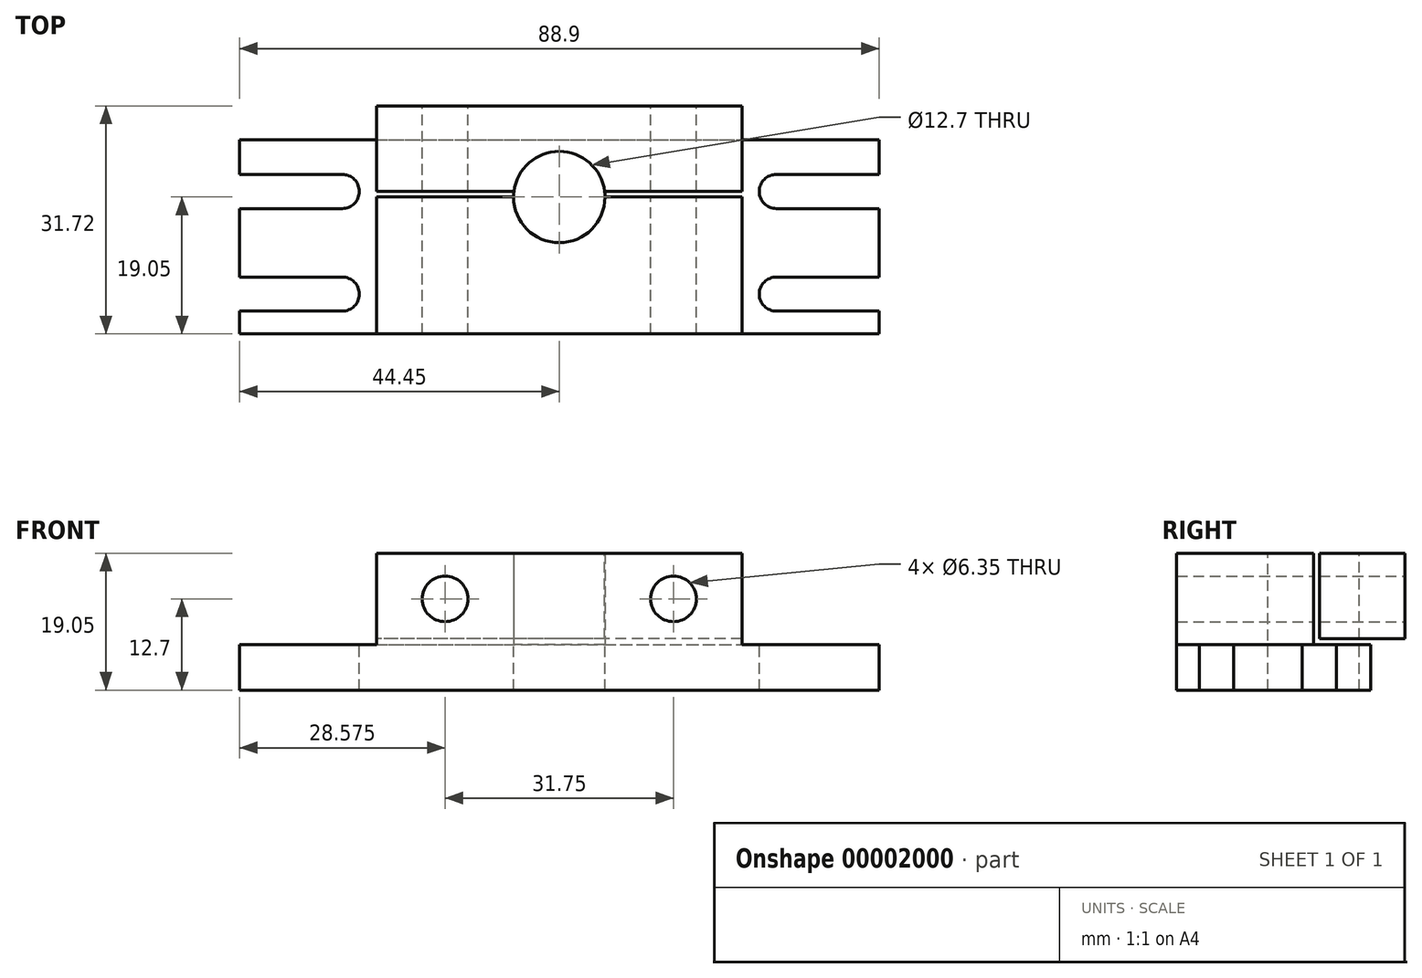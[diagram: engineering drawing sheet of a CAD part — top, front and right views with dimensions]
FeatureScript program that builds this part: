
annotation { "Feature Type Name" : "Feature", "Feature Type Description" : "" }
export const myFeature = defineFeature(function(context is Context, id is Id, definition is map)
    precondition{}
    {
        {
            var Q0;
            Q0=qCreatedBy(makeId("Top.planeOp"),FACE);
            var sketch = newSketch(context, id + "F0", { "sketchPlane" : qUnion([Q0])});
            skLineSegment(sketch, "E0.bottom", {"start": v(-44.45, 12.7) * mm, "end": v(44.45, 12.7) * mm});
            skLineSegment(sketch, "E0.top", {"start": v(-44.45, -12.7) * mm, "end": v(44.45, -12.7) * mm});
            skLineSegment(sketch, "E0.left", {"start": v(-44.45, 12.7) * mm, "end": v(-44.45, -12.7) * mm});
            skLineSegment(sketch, "E0.right", {"start": v(44.45, 12.7) * mm, "end": v(44.45, -12.7) * mm});
            skLineSegment(sketch, "E1", {"start": v(0, 12.7) * mm, "end": v(0, 0) * mm, "construction": true});
            skLineSegment(sketch, "E2", {"start": v(0, 0) * mm, "end": v(-44.45, 0) * mm, "construction": true});
            skSolve(sketch);
        }
        {
            var Q0;
            Q0=qSketchRegion(id+"F0",true);
            extrude(context, id + "F1", {"entities" : qUnion([Q0]), "depth" : 19.05 * mm});
        }
        {
            var Q0;
            Q0=makeQuery(id+"F1.opExtrude","SWEPT_FACE",FACE,{"disambiguationData":[OSD([sQuery(id+"F0.wireOp",EDGE,"E0.top")])]});
            var sketch = newSketch(context, id + "F2", { "sketchPlane" : qUnion([Q0])});
            skLineSegment(sketch, "E3.bottom", {"start": v(25.4, 19.05) * mm, "end": v(44.45, 19.05) * mm});
            skLineSegment(sketch, "E3.top", {"start": v(25.4, 6.35) * mm, "end": v(44.45, 6.35) * mm});
            skLineSegment(sketch, "E3.left", {"start": v(25.4, 19.05) * mm, "end": v(25.4, 6.35) * mm});
            skLineSegment(sketch, "E3.right", {"start": v(44.45, 19.05) * mm, "end": v(44.45, 6.35) * mm});
            skLineSegment(sketch, "E4.0.MirrorCS", {"start": v(-44.45, 19.05) * mm, "end": v(-44.45, 6.35) * mm});
            skLineSegment(sketch, "E4.1.MirrorCS", {"start": v(-25.4, 19.05) * mm, "end": v(-25.4, 6.35) * mm});
            skLineSegment(sketch, "E4.2.MirrorCS", {"start": v(-25.4, 19.05) * mm, "end": v(-44.45, 19.05) * mm});
            skLineSegment(sketch, "E4.3.MirrorCS", {"start": v(-25.4, 6.35) * mm, "end": v(-44.45, 6.35) * mm});
            skSolve(sketch);
        }
        {
            var Q0;
            Q0=qSketchRegion(id+"F2",true);
            var Q1;
            Q1=makeQuery(id+"F1.opExtrude","SWEPT_FACE",FACE,{"disambiguationData":[OSD([sQuery(id+"F0.wireOp",EDGE,"E0.bottom")])]});
            extrude(context, id + "F3", {"entities" : qUnion([Q0]), "operationType" : NewBodyOperationType.REMOVE, "endBound" : BoundingType.UP_TO_SURFACE, "oppositeDirection" : true, "endBoundEntityFace" : qUnion([Q1]), "depth" : 25.4 * mm});
        }
        {
            var Q0;
            Q0=makeQuery(id+"F3.boolean.opBoolean","COPY",FACE,{"derivedFrom":makeQuery(id+"F3.opExtrude","SWEPT_FACE",FACE,{"disambiguationData":[OSD([sQuery(id+"F2.wireOp",EDGE,"E3.left")])]})});
            var sketch = newSketch(context, id + "F4", { "sketchPlane" : qUnion([Q0])});
            skLineSegment(sketch, "E5.bottom", {"start": v(6.35, 19.05) * mm, "end": v(12.7, 19.05) * mm});
            skLineSegment(sketch, "E5.top", {"start": v(6.35, 6.35) * mm, "end": v(12.7, 6.35) * mm});
            skLineSegment(sketch, "E5.left", {"start": v(6.35, 19.05) * mm, "end": v(6.35, 6.35) * mm});
            skLineSegment(sketch, "E5.right", {"start": v(12.7, 19.05) * mm, "end": v(12.7, 6.35) * mm});
            skSolve(sketch);
        }
        {
            var Q0;
            Q0=qSketchRegion(id+"F4",true);
            var Q1;
            Q1=makeQuery(id+"F3.boolean.opBoolean","COPY",FACE,{"derivedFrom":makeQuery(id+"F3.opExtrude","SWEPT_FACE",FACE,{"disambiguationData":[OSD([sQuery(id+"F2.wireOp",EDGE,"E4.1.MirrorCS")])]})});
            extrude(context, id + "F5", {"entities" : qUnion([Q0]), "operationType" : NewBodyOperationType.REMOVE, "endBound" : BoundingType.UP_TO_SURFACE, "oppositeDirection" : true, "endBoundEntityFace" : qUnion([Q1]), "depth" : 25.4 * mm});
        }
        {
            var Q0;
            Q0=makeQuery(id+"F1.opExtrude","SWEPT_FACE",FACE,{"disambiguationData":[OSD([sQuery(id+"F0.wireOp",EDGE,"E0.bottom")])]});
            extrude(context, id + "F6", {"entities" : qUnion([Q0]), "operationType" : NewBodyOperationType.ADD, "depth" : 1.59 * mm});
        }
        {
            var Q0;
            {var subQ0=sQuery(id+"F2.wireOp",EDGE,"E3.top");var subQ1=sQuery(id+"F2.wireOp",EDGE,"E4.3.MirrorCS");var subQ2=sQuery(id+"F4.wireOp",EDGE,"E5.top");Q0=makeQuery(id+"F6.boolean.opBoolean","MERGE",FACE,{"derivedFrom":[makeQuery(id+"F5.boolean.opBoolean","MERGE",FACE,{"derivedFrom":[makeQuery(id+"F3.boolean.opBoolean","COPY",FACE,{"derivedFrom":makeQuery(id+"F3.opExtrude","SWEPT_FACE",FACE,{"disambiguationData":[OSD([subQ0])]})}),makeQuery(id+"F3.boolean.opBoolean","COPY",FACE,{"derivedFrom":makeQuery(id+"F3.opExtrude","SWEPT_FACE",FACE,{"disambiguationData":[OSD([subQ1])]})}),makeQuery(id+"F5.opExtrude","SWEPT_FACE",FACE,{"disambiguationData":[OSD([subQ2])]})]}),makeQuery(id+"F6.opExtrude","SWEPT_FACE",FACE,{"disambiguationData":[OSD([subQ0,subQ1,subQ2,sQuery(id+"F4.wireOp",EDGE,"E5.right")])]})]});}
            var sketch = newSketch(context, id + "F7", { "sketchPlane" : qUnion([Q0])});
            skCircle(sketch, "E6", {"center": v(0, 6.35) * mm, "radius": 6.35 * mm});
            skSolve(sketch);
        }
        {
            var Q0;
            Q0=qSketchRegion(id+"F7",true);
            var Q1;
            {var subQ0=sQuery(id+"F0.wireOp",EDGE,"E0.bottom");Q1=makeQuery(id+"F6.boolean.opBoolean","MERGE",FACE,{"derivedFrom":[makeQuery(id+"F1.opExtrude","CAP_FACE",FACE,{"disambiguationData":[OSD([subQ0,sQuery(id+"F0.wireOp",EDGE,"E0.top"),sQuery(id+"F0.wireOp",EDGE,"E0.left"),sQuery(id+"F0.wireOp",EDGE,"E0.right")])],"isStart":true}),makeQuery(id+"F6.opExtrude","SWEPT_FACE",FACE,{"disambiguationData":[OSD([subQ0])]})]});}
            extrude(context, id + "F8", {"entities" : qUnion([Q0]), "operationType" : NewBodyOperationType.REMOVE, "endBound" : BoundingType.UP_TO_SURFACE, "oppositeDirection" : true, "endBoundEntityFace" : qUnion([Q1]), "depth" : 25.4 * mm});
        }
        {
            var Q0;
            Q0=qSketchRegion(id+"F7",true);
            var Q1;
            Q1=makeQuery(id+"F1.opExtrude","CAP_FACE",FACE,{"disambiguationData":[OSD([sQuery(id+"F0.wireOp",EDGE,"E0.bottom"),sQuery(id+"F0.wireOp",EDGE,"E0.top"),sQuery(id+"F0.wireOp",EDGE,"E0.left"),sQuery(id+"F0.wireOp",EDGE,"E0.right")])],"isStart":false});
            extrude(context, id + "F9", {"entities" : qUnion([Q0]), "operationType" : NewBodyOperationType.REMOVE, "endBound" : BoundingType.UP_TO_SURFACE, "endBoundEntityFace" : qUnion([Q1]), "depth" : 25.4 * mm});
        }
        {
            var Q0;
            Q0=makeQuery(id+"F9.boolean.opBoolean","SPLIT",FACE,{"disambiguationData":[TD([makeQuery(id+"F3.boolean.opBoolean","COPY",FACE,{"derivedFrom":makeQuery(id+"F3.opExtrude","SWEPT_FACE",FACE,{"disambiguationData":[OSD([sQuery(id+"F2.wireOp",EDGE,"E3.left")])]})})])],"derivedFrom":makeQuery(id+"F5.boolean.opBoolean","COPY",FACE,{"derivedFrom":makeQuery(id+"F5.opExtrude","SWEPT_FACE",FACE,{"disambiguationData":[OSD([sQuery(id+"F4.wireOp",EDGE,"E5.left")])]})})});
            var sketch = newSketch(context, id + "F10", { "sketchPlane" : qUnion([Q0])});
            skCircle(sketch, "E7", {"center": v(-15.87, 12.7) * mm, "radius": 3.18 * mm});
            skLineSegment(sketch, "E8", {"start": v(-25.4, 12.7) * mm, "end": v(-15.87, 12.7) * mm, "construction": true});
            skLineSegment(sketch, "E9", {"start": v(-15.87, 19.05) * mm, "end": v(-15.87, 12.7) * mm, "construction": true});
            skCircle(sketch, "E10.0.MirrorC", {"center": v(15.87, 12.7) * mm, "radius": 3.18 * mm});
            skSolve(sketch);
        }
        {
            var Q0;
            Q0=qSketchRegion(id+"F10",true);
            var Q1;
            Q1=makeQuery(id+"F1.opExtrude","SWEPT_FACE",FACE,{"disambiguationData":[OSD([sQuery(id+"F0.wireOp",EDGE,"E0.top")])]});
            extrude(context, id + "F11", {"entities" : qUnion([Q0]), "operationType" : NewBodyOperationType.REMOVE, "endBound" : BoundingType.UP_TO_SURFACE, "oppositeDirection" : true, "endBoundEntityFace" : qUnion([Q1]), "depth" : 25.4 * mm});
        }
        {
            var Q0;
            Q0=makeQuery(id+"F9.boolean.opBoolean","SPLIT",FACE,{"disambiguationData":[TD([makeQuery(id+"F3.boolean.opBoolean","COPY",FACE,{"derivedFrom":makeQuery(id+"F3.opExtrude","SWEPT_FACE",FACE,{"disambiguationData":[OSD([sQuery(id+"F2.wireOp",EDGE,"E3.left")])]})})])],"derivedFrom":makeQuery(id+"F5.boolean.opBoolean","COPY",FACE,{"derivedFrom":makeQuery(id+"F5.opExtrude","SWEPT_FACE",FACE,{"disambiguationData":[OSD([sQuery(id+"F4.wireOp",EDGE,"E5.left")])]})})});
            cPlane(context, id + "F12", {"entities" : qUnion([Q0]), "cplaneType" : CPlaneType.OFFSET, "offset" : 0.79 * mm, "width" : 152.4 * mm, "height" : 152.4 * mm});
        }
        {
            var Q0;
            Q0=qCreatedBy(id+"F12.planeOp",FACE);
            var sketch = newSketch(context, id + "F13", { "sketchPlane" : qUnion([Q0])});
            skLineSegment(sketch, "E11.bottom", {"start": v(-25.4, 19.05) * mm, "end": v(25.4, 19.05) * mm});
            skLineSegment(sketch, "E11.top", {"start": v(-25.4, 7.14) * mm, "end": v(25.4, 7.14) * mm});
            skLineSegment(sketch, "E11.left", {"start": v(-25.4, 19.05) * mm, "end": v(-25.4, 7.14) * mm});
            skLineSegment(sketch, "E11.right", {"start": v(25.4, 19.05) * mm, "end": v(25.4, 7.14) * mm});
            skSolve(sketch);
        }
        {
            var Q0;
            Q0=qSketchRegion(id+"F13",true);
            extrude(context, id + "F14", {"entities" : qUnion([Q0]), "depth" : 11.9 * mm});
        }
        {
            var Q0;
            Q0=makeQuery(id+"F14.opExtrude","SWEPT_FACE",FACE,{"disambiguationData":[OSD([sQuery(id+"F13.wireOp",EDGE,"E11.bottom")])]});
            var sketch = newSketch(context, id + "F15", { "sketchPlane" : qUnion([Q0])});
            skArc(sketch, "E12", {"start": v(6.3, 7.14) * mm, "mid": v(0, 12.7) * mm, "end": v(-6.3, 7.14) * mm});
            skLineSegment(sketch, "E13", {"start": v(-6.3, 7.14) * mm, "end": v(6.3, 7.14) * mm});
            skSolve(sketch);
        }
        {
            var Q0;
            Q0=qSketchRegion(id+"F15",true);
            var Q1;
            Q1=makeQuery(id+"F14.opExtrude","SWEPT_FACE",FACE,{"disambiguationData":[OSD([sQuery(id+"F13.wireOp",EDGE,"E11.top")])]});
            extrude(context, id + "F16", {"entities" : qUnion([Q0]), "operationType" : NewBodyOperationType.REMOVE, "endBound" : BoundingType.UP_TO_SURFACE, "oppositeDirection" : true, "endBoundEntityFace" : qUnion([Q1]), "depth" : 25.4 * mm});
        }
        {
            var Q0;
            Q0=makeQuery(id+"F14.opExtrude","CAP_FACE",FACE,{"disambiguationData":[OSD([sQuery(id+"F13.wireOp",EDGE,"E11.bottom"),sQuery(id+"F13.wireOp",EDGE,"E11.top"),sQuery(id+"F13.wireOp",EDGE,"E11.left"),sQuery(id+"F13.wireOp",EDGE,"E11.right")])],"isStart":false});
            var sketch = newSketch(context, id + "F17", { "sketchPlane" : qUnion([Q0])});
            skCircle(sketch, "E14", {"center": v(-15.87, 12.7) * mm, "radius": 3.18 * mm});
            skCircle(sketch, "E15", {"center": v(15.87, 12.7) * mm, "radius": 3.18 * mm});
            skSolve(sketch);
        }
        {
            var Q0;
            Q0=qSketchRegion(id+"F17",true);
            var Q1;
            {var subQ0=sQuery(id+"F13.wireOp",EDGE,"E11.bottom");var subQ1=sQuery(id+"F13.wireOp",EDGE,"E11.top");var subQ2=sQuery(id+"F13.wireOp",EDGE,"E11.left");Q1=makeQuery(id+"F16.boolean.opBoolean","SPLIT",FACE,{"disambiguationData":[TD([makeQuery(id+"F14.opExtrude","SWEPT_FACE",FACE,{"disambiguationData":[OSD([subQ2])]})])],"derivedFrom":makeQuery(id+"F14.opExtrude","CAP_FACE",FACE,{"disambiguationData":[OSD([subQ0,subQ1,subQ2,sQuery(id+"F13.wireOp",EDGE,"E11.right")])],"isStart":true})});}
            extrude(context, id + "F18", {"entities" : qUnion([Q0]), "operationType" : NewBodyOperationType.REMOVE, "endBound" : BoundingType.UP_TO_SURFACE, "oppositeDirection" : true, "endBoundEntityFace" : qUnion([Q1]), "depth" : 25.4 * mm});
        }
        {
            var Q0;
            {var subQ0=sQuery(id+"F2.wireOp",EDGE,"E3.top");var subQ1=sQuery(id+"F2.wireOp",EDGE,"E4.3.MirrorCS");var subQ2=sQuery(id+"F4.wireOp",EDGE,"E5.top");Q0=makeQuery(id+"F6.boolean.opBoolean","MERGE",FACE,{"derivedFrom":[makeQuery(id+"F5.boolean.opBoolean","MERGE",FACE,{"derivedFrom":[makeQuery(id+"F3.boolean.opBoolean","COPY",FACE,{"derivedFrom":makeQuery(id+"F3.opExtrude","SWEPT_FACE",FACE,{"disambiguationData":[OSD([subQ0])]})}),makeQuery(id+"F3.boolean.opBoolean","COPY",FACE,{"derivedFrom":makeQuery(id+"F3.opExtrude","SWEPT_FACE",FACE,{"disambiguationData":[OSD([subQ1])]})}),makeQuery(id+"F5.opExtrude","SWEPT_FACE",FACE,{"disambiguationData":[OSD([subQ2])]})]}),makeQuery(id+"F6.opExtrude","SWEPT_FACE",FACE,{"disambiguationData":[OSD([subQ0,subQ1,subQ2,sQuery(id+"F4.wireOp",EDGE,"E5.right")])]})]});}
            var sketch = newSketch(context, id + "F19", { "sketchPlane" : qUnion([Q0])});
            skLineSegment(sketch, "E16", {"start": v(-44.45, -4.78) * mm, "end": v(-44.45, -9.52) * mm});
            skLineSegment(sketch, "E17", {"start": v(-44.45, -9.52) * mm, "end": v(-30.18, -9.52) * mm});
            skArc(sketch, "E18", {"start": v(-30.18, -9.52) * mm, "mid": v(-27.8, -7.15) * mm, "end": v(-30.18, -4.78) * mm});
            skLineSegment(sketch, "E19", {"start": v(-44.45, -4.78) * mm, "end": v(-30.18, -4.78) * mm});
            skLineSegment(sketch, "E20", {"start": v(-44.45, 9.5) * mm, "end": v(-44.45, 4.75) * mm});
            skLineSegment(sketch, "E21", {"start": v(-44.45, 4.75) * mm, "end": v(-30.18, 4.75) * mm});
            skLineSegment(sketch, "E22", {"start": v(-44.45, 9.5) * mm, "end": v(-30.18, 9.5) * mm});
            skArc(sketch, "E23", {"start": v(-30.18, 4.75) * mm, "mid": v(-27.8, 7.12) * mm, "end": v(-30.18, 9.5) * mm});
            skLineSegment(sketch, "E24.0.MirrorCS", {"start": v(44.45, 4.75) * mm, "end": v(30.18, 4.75) * mm});
            skLineSegment(sketch, "E24.1.MirrorCS", {"start": v(44.45, 9.5) * mm, "end": v(30.18, 9.5) * mm});
            skArc(sketch, "E24.2.MirrorCS", {"start": v(30.18, 4.75) * mm, "mid": v(27.8, 7.12) * mm, "end": v(30.18, 9.5) * mm});
            skLineSegment(sketch, "E24.3.MirrorCS", {"start": v(44.45, -9.52) * mm, "end": v(30.18, -9.52) * mm});
            skLineSegment(sketch, "E24.4.MirrorCS", {"start": v(44.45, -4.78) * mm, "end": v(44.45, -9.52) * mm});
            skArc(sketch, "E24.5.MirrorCS", {"start": v(30.18, -9.52) * mm, "mid": v(27.8, -7.15) * mm, "end": v(30.18, -4.78) * mm});
            skLineSegment(sketch, "E24.6.MirrorCS", {"start": v(44.45, 9.5) * mm, "end": v(44.45, 4.75) * mm});
            skLineSegment(sketch, "E24.7.MirrorCS", {"start": v(44.45, -4.78) * mm, "end": v(30.18, -4.78) * mm});
            skSolve(sketch);
        }
        {
            var Q0;
            Q0=qSketchRegion(id+"F19",true);
            var Q1;
            {var subQ0=sQuery(id+"F0.wireOp",EDGE,"E0.bottom");Q1=makeQuery(id+"F6.boolean.opBoolean","MERGE",FACE,{"derivedFrom":[makeQuery(id+"F1.opExtrude","CAP_FACE",FACE,{"disambiguationData":[OSD([subQ0,sQuery(id+"F0.wireOp",EDGE,"E0.top"),sQuery(id+"F0.wireOp",EDGE,"E0.left"),sQuery(id+"F0.wireOp",EDGE,"E0.right")])],"isStart":true}),makeQuery(id+"F6.opExtrude","SWEPT_FACE",FACE,{"disambiguationData":[OSD([subQ0])]})]});}
            extrude(context, id + "F20", {"entities" : qUnion([Q0]), "operationType" : NewBodyOperationType.REMOVE, "endBound" : BoundingType.UP_TO_SURFACE, "oppositeDirection" : true, "endBoundEntityFace" : qUnion([Q1]), "depth" : 25.4 * mm});
        }
    });
